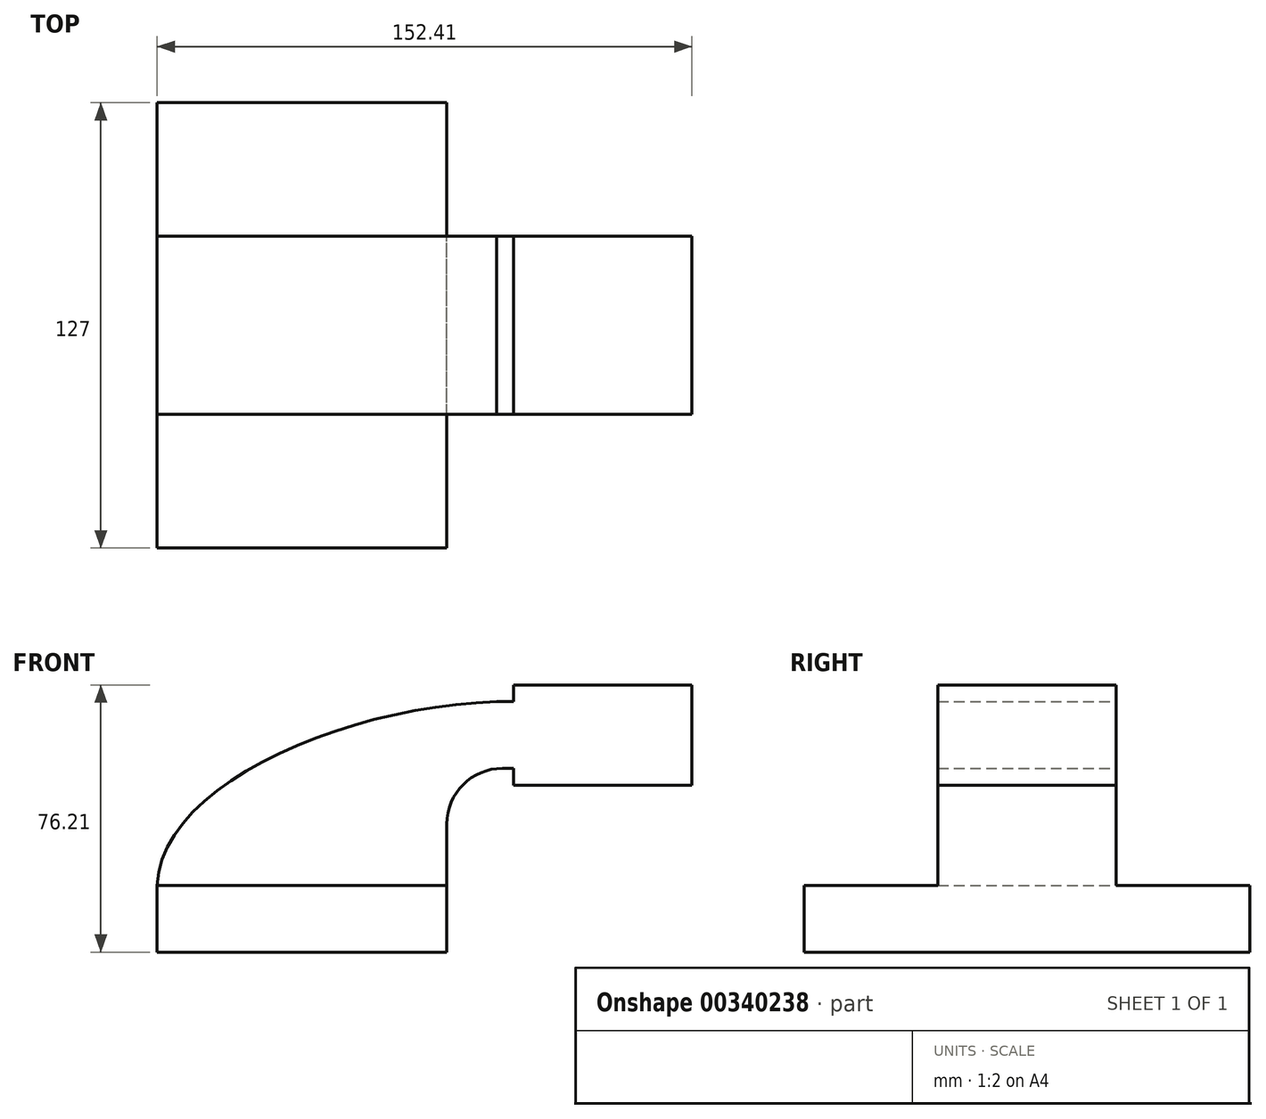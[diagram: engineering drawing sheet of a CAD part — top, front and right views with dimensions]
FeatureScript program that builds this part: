
annotation { "Feature Type Name" : "Feature", "Feature Type Description" : "" }
export const myFeature = defineFeature(function(context is Context, id is Id, definition is map)
    precondition{}
    {
        {
            var Q0;
            Q0=qCreatedBy(makeId("Front.planeOp"),FACE);
            var sketch = newSketch(context, id + "F0", { "sketchPlane" : qUnion([Q0])});
            skLineSegment(sketch, "E0.bottom", {"start": v(41.27, 9.53) * mm, "end": v(-41.28, 9.53) * mm});
            skLineSegment(sketch, "E0.top", {"start": v(41.28, -9.52) * mm, "end": v(-41.27, -9.52) * mm});
            skLineSegment(sketch, "E0.left", {"start": v(41.28, 9.53) * mm, "end": v(41.28, -9.52) * mm});
            skLineSegment(sketch, "E0.right", {"start": v(-41.28, 9.53) * mm, "end": v(-41.27, -9.52) * mm});
            skPoint(sketch, "E0.middle", {"position": v(0, 0) * mm});
            skLineSegment(sketch, "E1.bottom", {"start": v(111.12, 66.68) * mm, "end": v(60.32, 66.68) * mm});
            skLineSegment(sketch, "E1.top", {"start": v(111.12, 38.1) * mm, "end": v(60.33, 38.1) * mm});
            skLineSegment(sketch, "E1.left", {"start": v(111.13, 66.68) * mm, "end": v(111.13, 38.1) * mm});
            skLineSegment(sketch, "E1.right", {"start": v(60.32, 66.68) * mm, "end": v(60.33, 38.1) * mm});
            skPoint(sketch, "E1.middle", {"position": v(85.73, 52.39) * mm});
            skLineSegment(sketch, "E2", {"start": v(41.27, 9.53) * mm, "end": v(41.27, 27) * mm});
            skArc(sketch, "E3", {"start": v(41.27, 27) * mm, "mid": v(45.92, 38.23) * mm, "end": v(57.15, 42.88) * mm});
            skLineSegment(sketch, "E4", {"start": v(57.15, 42.88) * mm, "end": v(85.73, 42.88) * mm});
            skLineSegment(sketch, "E5.0", {"start": v(57.15, 61.93) * mm, "end": v(85.27, 61.93) * mm});
            skArc(sketch, "E5.1", {"start": v(22.23, 27) * mm, "mid": v(32.45, 51.7) * mm, "end": v(57.15, 61.93) * mm});
            skLineSegment(sketch, "E5.2", {"start": v(22.22, 9.53) * mm, "end": v(22.22, 27) * mm});
            skFitSpline(sketch, "E6", {"points": [v(-41.28, 9.52) * mm, v(57.15, 61.93) * mm], "startDerivative": vector(3.19, 87.02) * mm, "endDerivative": vector(132.02, 2.46) * mm});
            skLineSegment(sketch, "E7", {"start": v(85.27, 61.93) * mm, "end": v(85.73, 42.88) * mm});
            skSolve(sketch);
        }
        {
            var Q0;
            Q0=makeQuery(id+"F0.imprint","IMPRINT",FACE,{"disambiguationData":[TD([[makeQuery(id+"F0.imprint","IMPRINT",EDGE,{"derivedFrom":sQuery(id+"F0.wireOp",EDGE,"E0.top")}),-1.0]])]});
            extrude(context, id + "F1", {"entities" : qUnion([Q0]), "endBound" : BoundingType.SYMMETRIC, "depth" : 127 * mm});
        }
        {
            var Q0;
            Q0 = qSketchRegion(id + "F0", true);
            extrude(context, id + "F2", {"entities" : qUnion([Q0]), "operationType" : NewBodyOperationType.ADD, "endBound" : BoundingType.SYMMETRIC, "depth" : 50.8 * mm});
        }
    });
